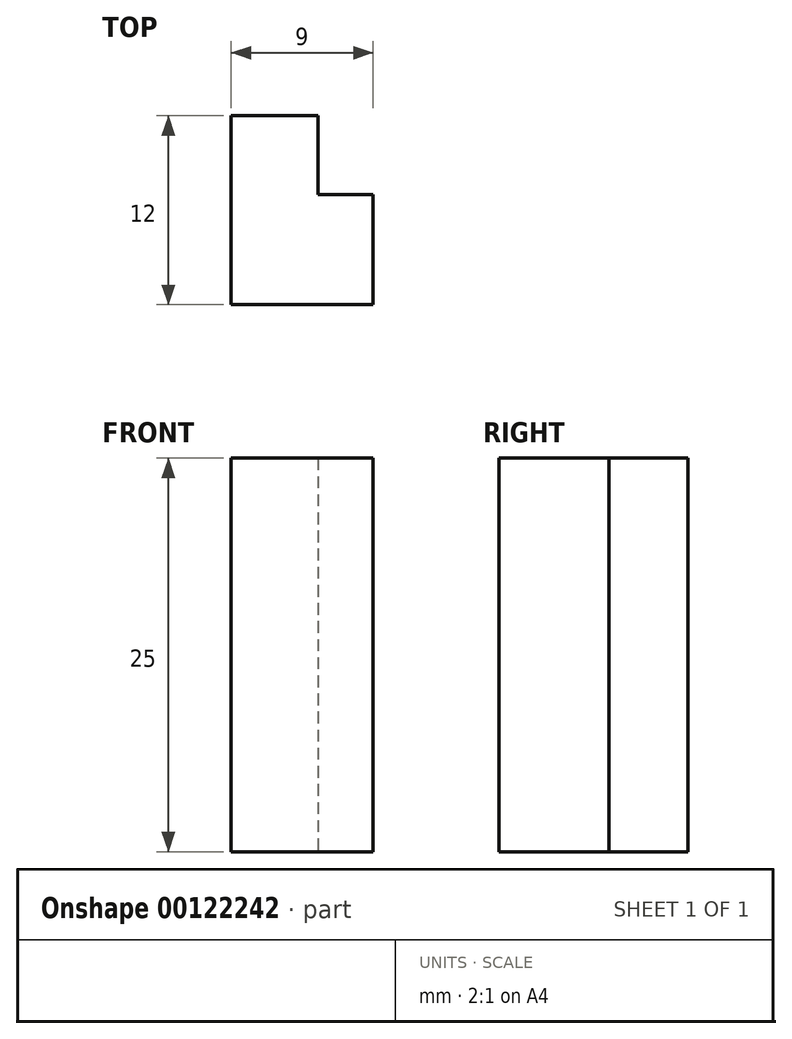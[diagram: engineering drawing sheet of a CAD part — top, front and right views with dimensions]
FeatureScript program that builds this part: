
annotation { "Feature Type Name" : "Feature", "Feature Type Description" : "" }
export const myFeature = defineFeature(function(context is Context, id is Id, definition is map)
    precondition{}
    {
        {
            var Q0;
            Q0=qCreatedBy(makeId("Top.planeOp"),FACE);
            var sketch = newSketch(context, id + "F0", { "sketchPlane" : qUnion([Q0])});
            skLineSegment(sketch, "E0", {"start": v(-33.83, 33.15) * mm, "end": v(-33.83, 21.15) * mm});
            skLineSegment(sketch, "E1", {"start": v(-33.83, 21.15) * mm, "end": v(-24.83, 21.15) * mm});
            skLineSegment(sketch, "E2", {"start": v(-24.83, 21.15) * mm, "end": v(-24.83, 28.15) * mm});
            skLineSegment(sketch, "E3", {"start": v(-33.83, 33.15) * mm, "end": v(-28.33, 33.15) * mm});
            skLineSegment(sketch, "E4", {"start": v(-28.33, 33.15) * mm, "end": v(-28.33, 28.15) * mm});
            skLineSegment(sketch, "E5", {"start": v(-28.33, 28.15) * mm, "end": v(-24.83, 28.15) * mm});
            skSolve(sketch);
        }
        {
            var Q0;
            Q0=makeQuery(id+"F0.imprint","IMPRINT",FACE,{"disambiguationData":[TD([[makeQuery(id+"F0.imprint","IMPRINT",EDGE,{"derivedFrom":sQuery(id+"F0.wireOp",EDGE,"E0")}),1.0]])]});
            extrude(context, id + "F1", {"entities" : qUnion([Q0]), "depth" : 25 * mm});
        }
    });
